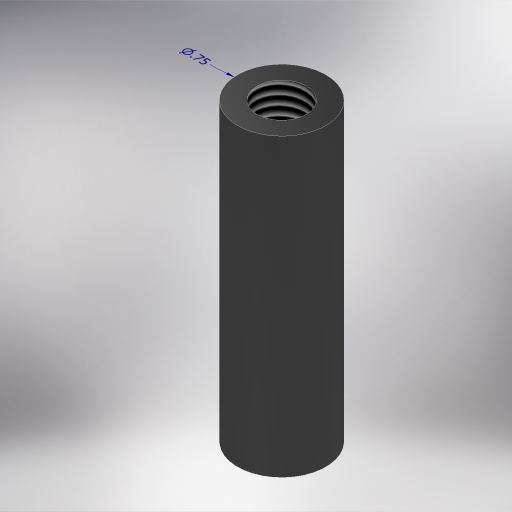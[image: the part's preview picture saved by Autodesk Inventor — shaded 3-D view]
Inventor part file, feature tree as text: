
AUTODESK INVENTOR PART (.ipt)
format: ipt  version: 2024 (Build 280153000, 153)  size: 304,640 bytes
history: native  units: in
note: dims shown in document units (in); Inventor stores cm internally (conversion verified against a paired STEP export)
features: other x2, extrude x1, hole x1
ambient origin geometry x8: Origin, YZ Plane, XZ Plane, XY Plane, X Axis, Y Axis, Z Axis, Center Point
bodies: Solid1 (feature_tree)
feature tree (4):
  other  "Annotations"
  extrude  "Extrusion1"  Depth=0.746in
  hole  "Hole1"  [1 undecoded]
  other  "Diameter Dimension 1"
note: 1 required parameter value undecoded (feature->parameter linkage not recoverable at this tier; creation-order binding heuristic only, values carry confidence <= 0.55)
